FCSTD DOCUMENT  (FreeCAD 0.19R)
Label: cafe_veloce
License: Other
LicenseURL: https://ohwr.org/project/cernohl/wikis/Documents/CERN-OHL-version-2
objects: Part::Compound2×9, Part::Feature×6, App::Link×6, App::LinkGroup×4, App::VRMLObject×1
note: 6 computed .brp shape members not serialized (recipe doc carries the construction recipe); baked Part::Feature solids carry a one-line shape summary decoded from their .brp

FEATURE [App::VRMLObject] veloce
  Placement = pos=(0,0,0) rot=(0,0,1;1.5708rad)
  Resources = veloce/Conn_Wurth_RA_16.wrl | veloce/ | veloce/ | veloce/ | veloce/ | veloce/ | veloce/ | veloce/
FEATURE [Part::Feature] Solid  label="ML-46BFN_ML-46BFN*15"
FEATURE [Part::Compound2] Compound  label="NAUO11"
  Links = -> [Solid]
FEATURE [Part::Feature] Solid001  label="INSERT-3_INSERT-3"
FEATURE [Part::Compound2] Compound001  label="NAUO12"
  Links = -> [Solid001]
  Placement = pos=(63.0963,20.7772,-45.3238) rot=(0,0,1;1.5708rad)
FEATURE [App::Link] Link  label="NAUO13"
  LinkPlacement = pos=(-63.0963,20.7772,-45.3238) rot=(0.643767,0.643767,-0.413677;3.92607rad)
  LinkedObject = -> Solid001
  Placement = pos=(-63.0963,20.7772,-45.3238) rot=(0.643767,0.643767,-0.413677;3.92607rad)
FEATURE [App::Link] Link001  label="NAUO14"
  LinkPlacement = pos=(-63.0963,20.7772,45.3238) rot=(0.643767,0.643767,-0.413677;3.92607rad)
  LinkedObject = -> Solid001
  Placement = pos=(-63.0963,20.7772,45.3238) rot=(0.643767,0.643767,-0.413677;3.92607rad)
FEATURE [App::Link] Link002  label="NAUO15"
  LinkPlacement = pos=(63.0963,20.7772,45.3238) rot=(0.643767,0.643767,-0.413677;3.92607rad)
  LinkedObject = -> Solid001
  Placement = pos=(63.0963,20.7772,45.3238) rot=(0.643767,0.643767,-0.413677;3.92607rad)
FEATURE [App::LinkGroup] LinkGroup  label="ML-46BF_ML-46BF*15"
  ElementList = -> [Compound,Compound001,Link,Link001,Link002]
  LinkMode = 0
FEATURE [Part::Compound2] Compound002  label="NAUO1"
  Links = -> [LinkGroup]
FEATURE [Part::Feature] Solid002  label="ML-46C_ML-46C*15"
FEATURE [Part::Compound2] Compound003  label="NAUO9"
  Links = -> [Solid002]
FEATURE [Part::Feature] Solid003  label="GASKET-5_GASKET-5"
FEATURE [Part::Compound2] Compound004  label="NAUO10"
  Links = -> [Solid003]
  Placement = pos=(0,4.064,0) rot=(0,0.707107,0.707107;3.14159rad)
FEATURE [App::LinkGroup] LinkGroup001  label="ML-46CG_ML-46CG*15"
  ElementList = -> [Compound003,Compound004]
  LinkMode = 0
FEATURE [Part::Compound2] Compound005  label="NAUO2"
  Links = -> [LinkGroup001]
  Placement = pos=(0,42.799,0) rot=(0,0,1;0rad)
FEATURE [Part::Feature] Solid004  label="ML-46BF-PCB_ML-46BF-PCB"
FEATURE [Part::Compound2] Compound006  label="NAUO3"
  Links = -> [Solid004]
  Placement = pos=(0,9.652,0) rot=(0,0,1;0rad)
FEATURE [Part::Feature] Solid005  label="SCREWS-SS6-32-1_SCREWS-SS6-32-1"
FEATURE [Part::Compound2] Compound007  label="NAUO5"
  Links = -> [Solid005]
  Placement = pos=(16.8374,-19.05,-2.78e-14) rot=(0,0,1;0rad)
FEATURE [App::Link] Link003  label="NAUO6"
  LinkPlacement = pos=(16.8374,-145.243,-2.84e-14) rot=(1,0,0;0.171038rad)
  LinkedObject = -> Solid005
  Placement = pos=(16.8374,-145.243,-2.84e-14) rot=(1,0,0;0.171038rad)
FEATURE [App::Link] Link004  label="NAUO7"
  LinkPlacement = pos=(16.8374,-145.243,90.6477) rot=(0,0,1;0rad)
  LinkedObject = -> Solid005
  Placement = pos=(16.8374,-145.243,90.6477) rot=(0,0,1;0rad)
FEATURE [App::Link] Link005  label="NAUO8"
  LinkPlacement = pos=(16.8374,-19.05,90.6477) rot=(-1,0,0;0.733606rad)
  LinkedObject = -> Solid005
  Placement = pos=(16.8374,-19.05,90.6477) rot=(-1,0,0;0.733606rad)
FEATURE [App::LinkGroup] LinkGroup002  label="SCREWS-SS6-4_SCREWS-SS6-4"
  ElementList = -> [Compound007,Link003,Link004,Link005]
  LinkMode = 0
FEATURE [Part::Compound2] Compound008  label="NAUO4"
  Links = -> [LinkGroup002]
  Placement = pos=(82.1463,70.1241,-45.3238) rot=(0,0,-1;1.5708rad)
FEATURE [App::LinkGroup] LinkGroup003  label="ML-46F"
  ElementList = -> [Compound002,Compound005,Compound006,Compound008]
  LinkMode = 0
  Placement = pos=(-50,50,-12) rot=(1,0,0;1.5708rad)
